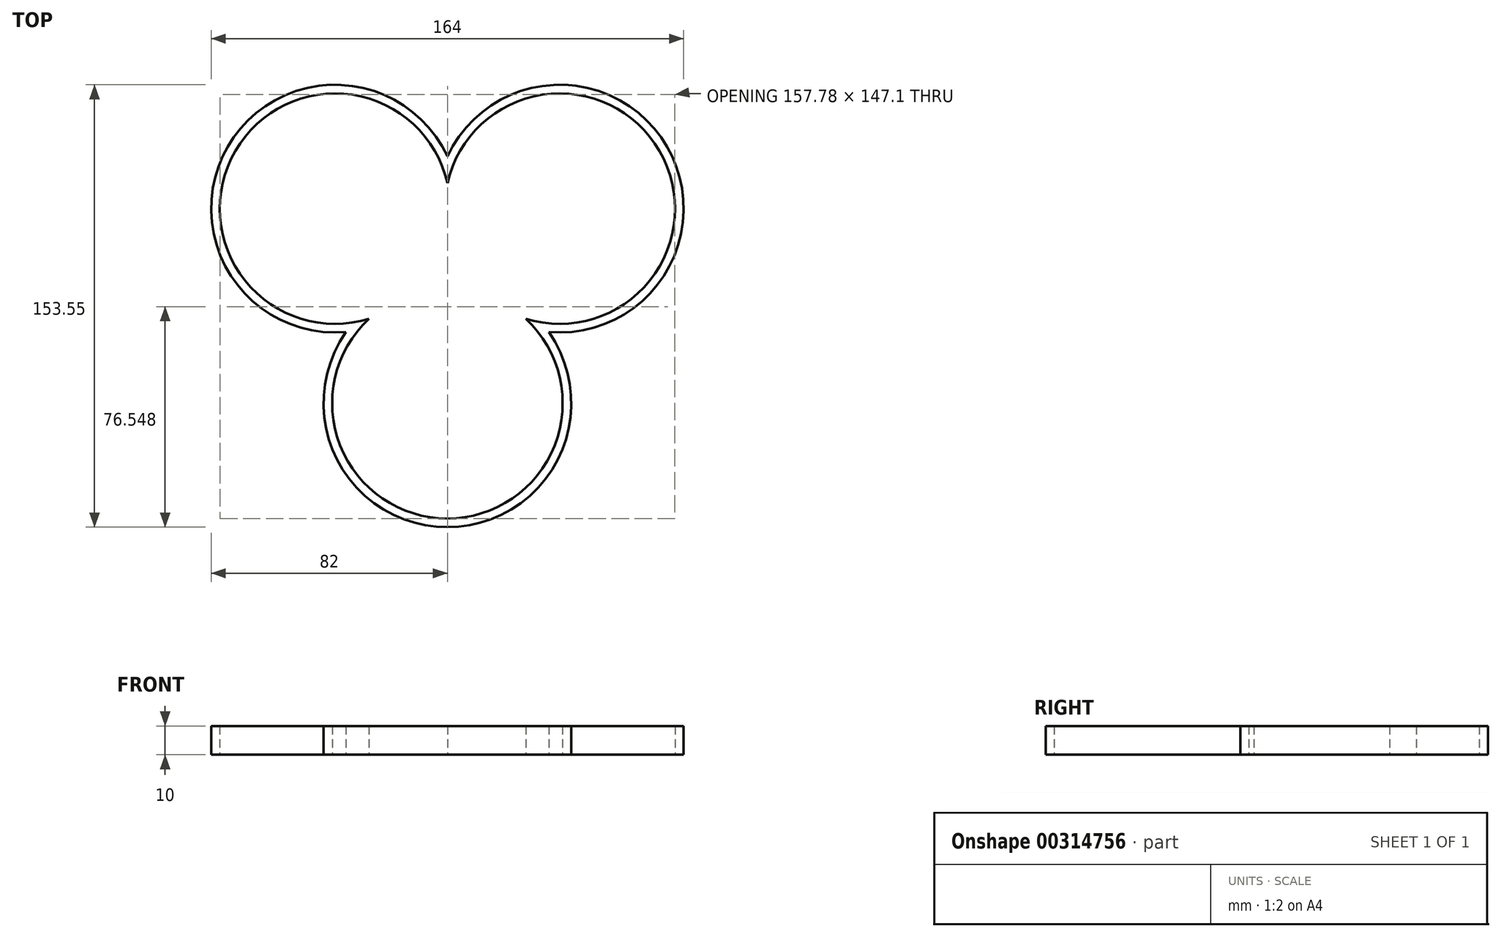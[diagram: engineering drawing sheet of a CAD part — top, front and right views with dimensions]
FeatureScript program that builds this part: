
annotation { "Feature Type Name" : "Feature", "Feature Type Description" : "" }
export const myFeature = defineFeature(function(context is Context, id is Id, definition is map)
    precondition{}
    {
        {
            var Q0;
            Q0=qCreatedBy(makeId("Top.planeOp"),FACE);
            var sketch = newSketch(context, id + "F0", { "sketchPlane" : qUnion([Q0])});
            skCircle(sketch, "E0.cCircle", {"center": v(0, 0) * mm, "radius": 22.52 * mm, "construction": true});
            skLineSegment(sketch, "E0.0", {"start": v(-39, 22.52) * mm, "end": v(39, 22.52) * mm, "construction": true});
            skLineSegment(sketch, "E0.1", {"start": v(39, 22.52) * mm, "end": v(0, -45.03) * mm, "construction": true});
            skLineSegment(sketch, "E0.2", {"start": v(0, -45.03) * mm, "end": v(-39, 22.52) * mm, "construction": true});
            skPoint(sketch, "E0.0.midPoint", {"position": v(0, 22.52) * mm});
            skArc(sketch, "E1", {"start": v(0, 31.4) * mm, "mid": v(-73.64, 42.52) * mm, "end": v(-27.2, -15.7) * mm});
            skArc(sketch, "E2", {"start": v(-1, 22.52) * mm, "mid": v(-1, 22.5) * mm, "end": v(-1, 22.5) * mm});
            skArc(sketch, "E3", {"start": v(-19.98, -10.38) * mm, "mid": v(-20, -10.39) * mm, "end": v(-20, -10.4) * mm});
            skArc(sketch, "E4.trimOffspring", {"start": v(1, 22.5) * mm, "mid": v(1, 22.5) * mm, "end": v(1, 22.52) * mm});
            skArc(sketch, "E5.trimOffspring", {"start": v(18.98, -12.11) * mm, "mid": v(19, -12.12) * mm, "end": v(19, -12.12) * mm});
            skArc(sketch, "E6.trimOffspring", {"start": v(27.2, -15.7) * mm, "mid": v(73.64, 42.52) * mm, "end": v(0, 31.4) * mm});
            skArc(sketch, "E7.trimOffspring", {"start": v(20, -10.4) * mm, "mid": v(20, -10.39) * mm, "end": v(19.98, -10.38) * mm});
            skArc(sketch, "E8.trimOffspring", {"start": v(-27.2, -15.7) * mm, "mid": v(0, -85.03) * mm, "end": v(27.2, -15.7) * mm});
            skArc(sketch, "E9.trimOffspring", {"start": v(-19, -12.12) * mm, "mid": v(-19, -12.12) * mm, "end": v(-18.98, -12.11) * mm});
            skArc(sketch, "E10.0", {"start": v(0, 40.63) * mm, "mid": v(-76.24, 44.02) * mm, "end": v(-35.18, -20.31) * mm});
            skArc(sketch, "E10.1", {"start": v(35.18, -20.31) * mm, "mid": v(76.24, 44.02) * mm, "end": v(0, 40.63) * mm});
            skArc(sketch, "E10.2", {"start": v(-35.18, -20.31) * mm, "mid": v(0, -88.03) * mm, "end": v(35.18, -20.31) * mm});
            skSolve(sketch);
        }
        {
            var Q0;
            Q0 = qSketchRegion(id + "F0", true);
            extrude(context, id + "F1", {"entities" : qUnion([Q0]), "depth" : 10 * mm});
        }
    });
